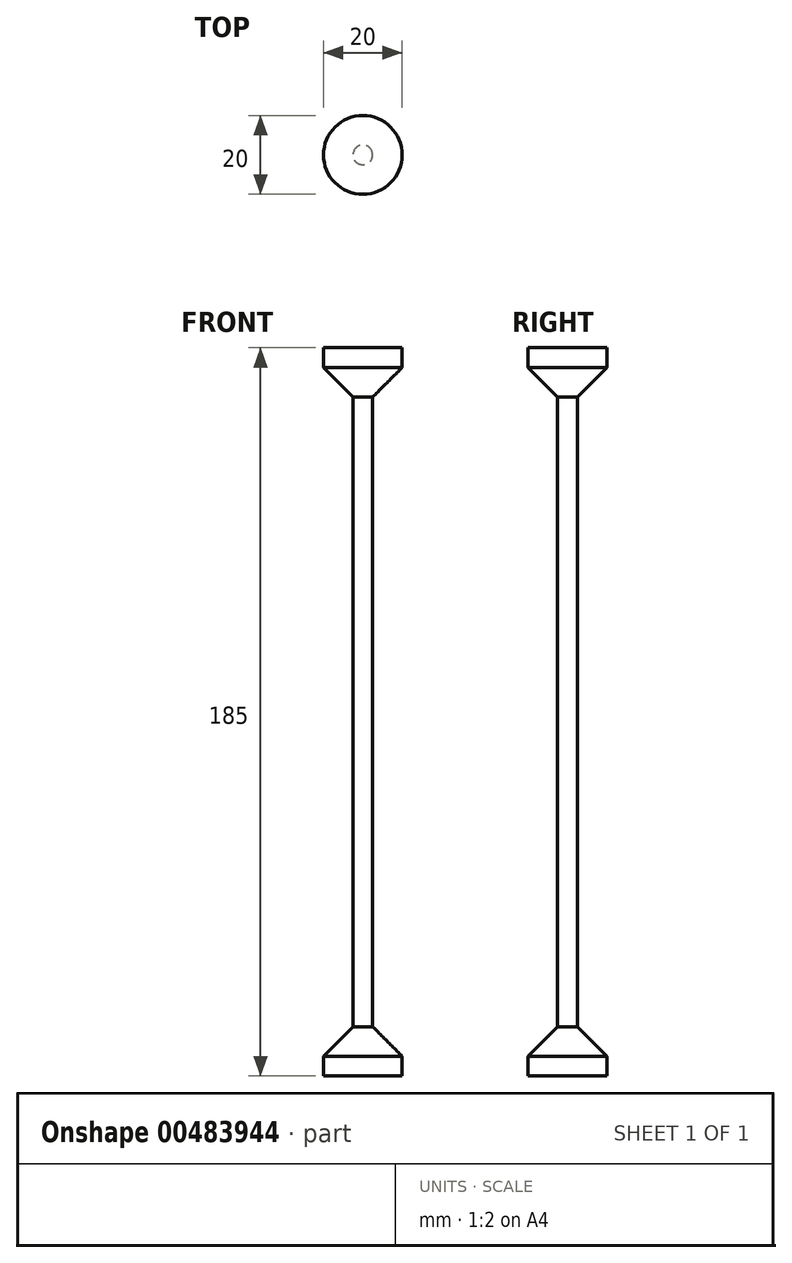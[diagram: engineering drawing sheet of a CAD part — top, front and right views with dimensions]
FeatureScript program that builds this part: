
annotation { "Feature Type Name" : "Feature", "Feature Type Description" : "" }
export const myFeature = defineFeature(function(context is Context, id is Id, definition is map)
    precondition{}
    {
        {
            var Q0;
            Q0=qCreatedBy(makeId("Front.planeOp"),FACE);
            var sketch = newSketch(context, id + "F0", { "sketchPlane" : qUnion([Q0])});
            skLineSegment(sketch, "E0", {"start": v(0, 0) * mm, "end": v(10, 0) * mm});
            skLineSegment(sketch, "E1", {"start": v(10, 0) * mm, "end": v(10, 5) * mm});
            skLineSegment(sketch, "E2", {"start": v(10, 5) * mm, "end": v(2.5, 12.5) * mm});
            skLineSegment(sketch, "E3", {"start": v(2.5, 12.5) * mm, "end": v(2.5, 172.5) * mm});
            skLineSegment(sketch, "E4", {"start": v(10, 185) * mm, "end": v(0, 185) * mm});
            skLineSegment(sketch, "E5", {"start": v(0, 185) * mm, "end": v(0, 0) * mm});
            skLineSegment(sketch, "E6", {"start": v(10, 185) * mm, "end": v(10, 180) * mm});
            skLineSegment(sketch, "E7", {"start": v(10, 180) * mm, "end": v(2.5, 172.5) * mm});
            skSolve(sketch);
        }
        {
            var Q0;
            Q0 = qSketchRegion(id + "F0", true);
            var Q1;
            Q1=sQuery(id+"F0.wireOp",EDGE,"E5");
            revolve(context, id + "F1", {"entities" : qUnion([Q0]), "axis" : qUnion([Q1]), "revolveType" : RevolveType.FULL});
        }
    });
